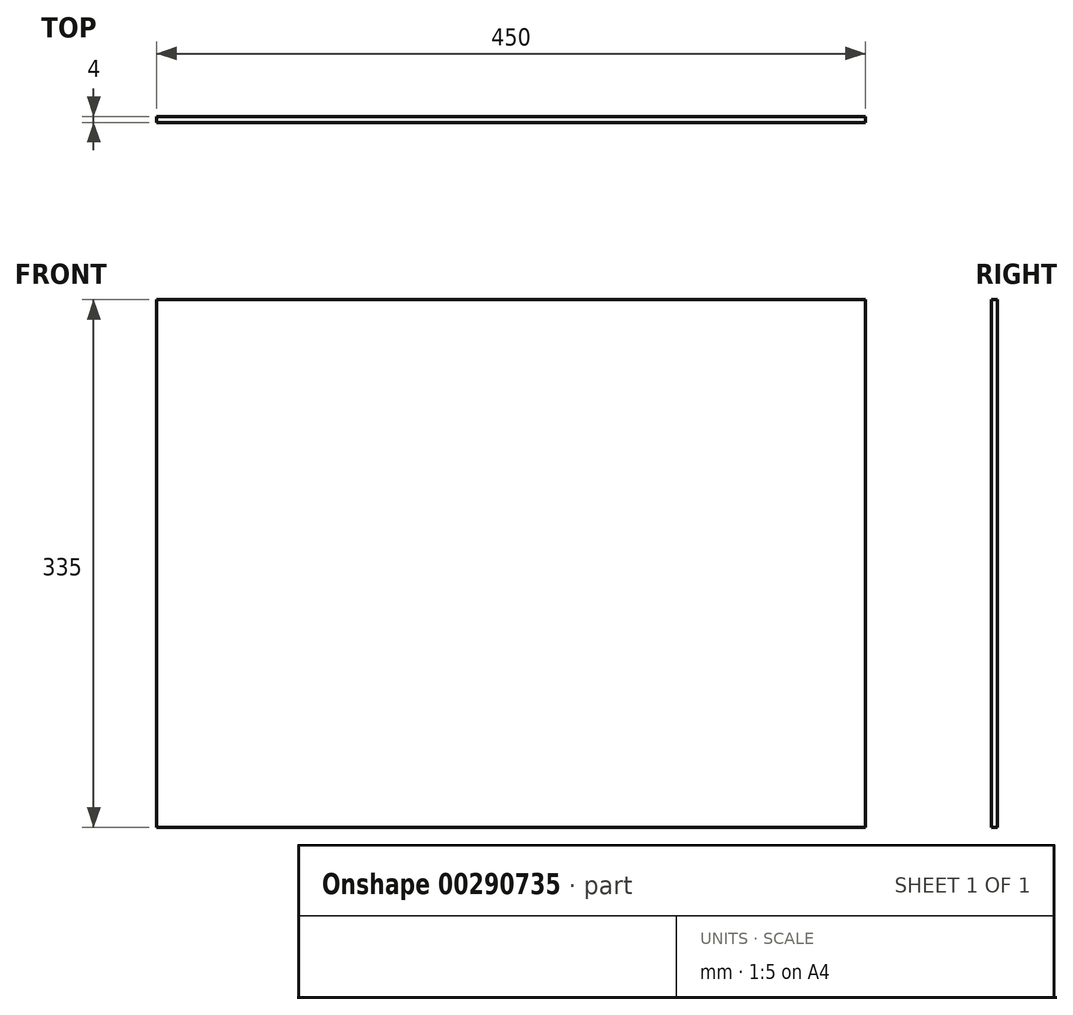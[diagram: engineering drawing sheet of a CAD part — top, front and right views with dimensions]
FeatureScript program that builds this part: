
annotation { "Feature Type Name" : "Feature", "Feature Type Description" : "" }
export const myFeature = defineFeature(function(context is Context, id is Id, definition is map)
    precondition{}
    {
        {
            var Q0;
            Q0=qCreatedBy(makeId("Front.planeOp"),FACE);
            var sketch = newSketch(context, id + "F1", { "sketchPlane" : qUnion([Q0])});
            skLineSegment(sketch, "E0.bottom", {"start": v(-223.44, 82.53) * mm, "end": v(226.56, 82.53) * mm});
            skLineSegment(sketch, "E0.top", {"start": v(-223.44, -252.47) * mm, "end": v(226.56, -252.47) * mm});
            skLineSegment(sketch, "E0.left", {"start": v(-223.44, 82.53) * mm, "end": v(-223.44, -252.47) * mm});
            skLineSegment(sketch, "E0.right", {"start": v(226.56, 82.53) * mm, "end": v(226.56, -252.47) * mm});
            skSolve(sketch);
        }
        {
            var Q0;
            Q0 = qSketchRegion(id + "F1", true);
            extrude(context, id + "F0", {"entities" : qUnion([Q0]), "depth" : 4 * mm});
        }
    });
